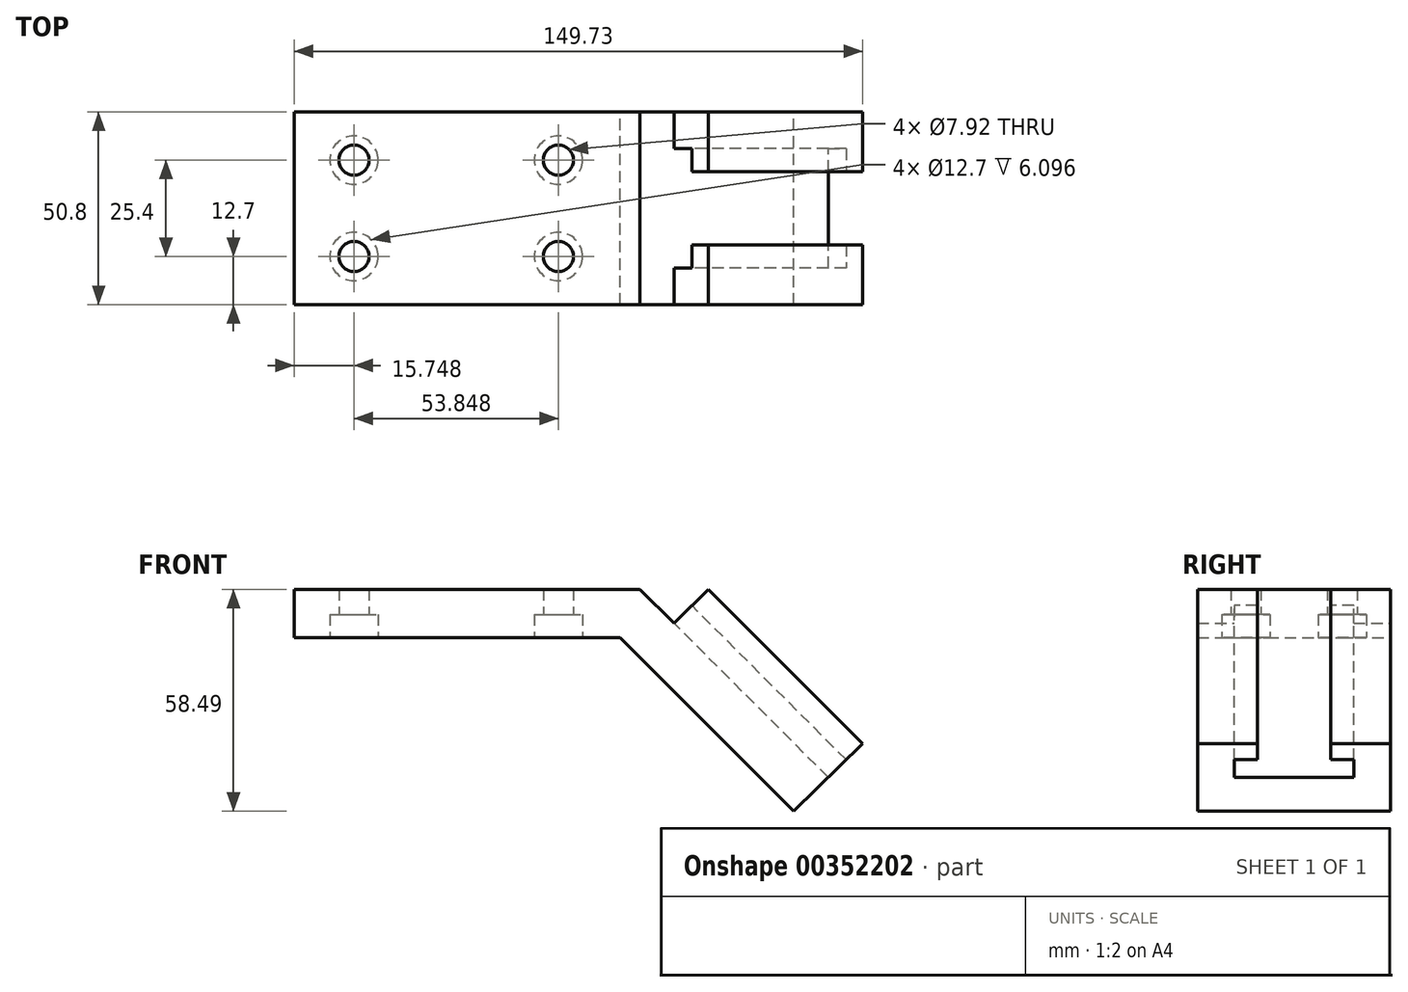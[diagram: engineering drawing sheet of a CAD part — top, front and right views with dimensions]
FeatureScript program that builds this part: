
annotation { "Feature Type Name" : "Feature", "Feature Type Description" : "" }
export const myFeature = defineFeature(function(context is Context, id is Id, definition is map)
    precondition{}
    {
        {
            var Q0;
            Q0=qCreatedBy(makeId("Front.planeOp"),FACE);
            var sketch = newSketch(context, id + "F0", { "sketchPlane" : qUnion([Q0])});
            skLineSegment(sketch, "E0", {"start": v(0, 0) * mm, "end": v(0, 12.7) * mm});
            skLineSegment(sketch, "E1", {"start": v(0, 12.7) * mm, "end": v(91.11, 12.7) * mm});
            skLineSegment(sketch, "E2", {"start": v(0, 0) * mm, "end": v(85.85, 0) * mm});
            skLineSegment(sketch, "E3", {"start": v(91.11, 12.7) * mm, "end": v(100.1, 3.72) * mm});
            skLineSegment(sketch, "E4", {"start": v(85.85, 0) * mm, "end": v(131.64, -45.79) * mm});
            skLineSegment(sketch, "E5", {"start": v(149.73, -27.96) * mm, "end": v(109.07, 12.7) * mm});
            skLineSegment(sketch, "E6", {"start": v(109.07, 12.7) * mm, "end": v(100.1, 3.72) * mm});
            skLineSegment(sketch, "E7", {"start": v(131.64, -45.79) * mm, "end": v(149.73, -27.96) * mm});
            skSolve(sketch);
        }
        {
            var Q0;
            Q0=makeQuery(id+"F0.imprint","IMPRINT",FACE,{"disambiguationData":[TD([[makeQuery(id+"F0.imprint","IMPRINT",EDGE,{"derivedFrom":sQuery(id+"F0.wireOp",EDGE,"E0")}),-1.0]])]});
            extrude(context, id + "F1", {"entities" : qUnion([Q0]), "depth" : 50.8 * mm});
        }
        {
            var Q0;
            Q0=qCreatedBy(makeId("Top.planeOp"),FACE);
            var sketch = newSketch(context, id + "F2", { "sketchPlane" : qUnion([Q0])});
            skCircle(sketch, "E8", {"center": v(15.75, -12.7) * mm, "radius": 3.96 * mm});
            skCircle(sketch, "E9", {"center": v(15.75, -38.1) * mm, "radius": 3.96 * mm});
            skCircle(sketch, "E10", {"center": v(69.6, -12.7) * mm, "radius": 3.96 * mm});
            skCircle(sketch, "E11", {"center": v(69.6, -38.1) * mm, "radius": 3.96 * mm});
            skSolve(sketch);
        }
        {
            var Q0;
            Q0=sQuery(id+"F2.wireOp",VERTEX,"E8.center");
            var Q1;
            Q1=sQuery(id+"F2.wireOp",VERTEX,"E9.center");
            var Q2;
            Q2=sQuery(id+"F2.wireOp",VERTEX,"E11.center");
            var Q3;
            Q3=sQuery(id+"F2.wireOp",VERTEX,"E10.center");
            var Q4;
            Q4=makeQuery(id+"F1.opExtrude","SWEPT_BODY",BODY,{"disambiguationData":[OSD([sQuery(id+"F0.wireOp",EDGE,"E0"),sQuery(id+"F0.wireOp",EDGE,"E1"),sQuery(id+"F0.wireOp",EDGE,"E2"),sQuery(id+"F0.wireOp",EDGE,"E3"),sQuery(id+"F0.wireOp",EDGE,"E4"),sQuery(id+"F0.wireOp",EDGE,"E5"),sQuery(id+"F0.wireOp",EDGE,"E6"),sQuery(id+"F0.wireOp",EDGE,"E7")])]});
            hole(context, id + "F3", {"style" : HoleStyle.C_BORE, "endStyle" : HoleEndStyle.THROUGH, "oppositeDirection" : true, "holeDiameter" : 7.92 * mm, "cBoreDiameter" : 12.7 * mm, "cBoreDepth" : 6.1 * mm, "isTappedThrough" : true, "tappedDepth" : 12.7 * mm, "tapClearance" : 3, "locations" : qUnion([Q0, Q1, Q2, Q3]), "scope" : qUnion([Q4])});
        }
        {
            var Q0;
            Q0=makeQuery(id+"F1.opExtrude","SWEPT_FACE",FACE,{"disambiguationData":[OSD([sQuery(id+"F0.wireOp",EDGE,"E5")])]});
            var sketch = newSketch(context, id + "F4", { "sketchPlane" : qUnion([Q0])});
            skArc(sketch, "E12", {"start": v(115.63, -50.8) * mm, "mid": v(122, -25.4) * mm, "end": v(115.63, 0) * mm});
            skLineSegment(sketch, "E13", {"start": v(115.63, -50.8) * mm, "end": v(125.64, -50.8) * mm});
            skLineSegment(sketch, "E14", {"start": v(125.64, -50.8) * mm, "end": v(125.64, 0) * mm});
            skLineSegment(sketch, "E15", {"start": v(125.64, 0) * mm, "end": v(115.63, 0) * mm});
            skSolve(sketch);
        }
        {
            var Q0;
            Q0 = qSketchRegion(id + "F4", true);
            extrude(context, id + "F5", {"entities" : qUnion([Q0]), "operationType" : NewBodyOperationType.REMOVE, "endBound" : BoundingType.THROUGH_ALL, "oppositeDirection" : true, "depth" : 25.4 * mm});
        }
        {
            var Q0;
            Q0=makeQuery(id+"F1.opExtrude","SWEPT_FACE",FACE,{"disambiguationData":[OSD([sQuery(id+"F0.wireOp",EDGE,"E6")])]});
            var sketch = newSketch(context, id + "F6", { "sketchPlane" : qUnion([Q0])});
            skLineSegment(sketch, "E16", {"start": v(41.15, 73.4) * mm, "end": v(9.65, 73.4) * mm});
            skLineSegment(sketch, "E17", {"start": v(9.65, 73.4) * mm, "end": v(9.65, 80) * mm});
            skLineSegment(sketch, "E18", {"start": v(9.65, 80) * mm, "end": v(15.75, 80) * mm});
            skLineSegment(sketch, "E19", {"start": v(15.75, 80) * mm, "end": v(15.75, 86.1) * mm});
            skLineSegment(sketch, "E20", {"start": v(15.75, 86.1) * mm, "end": v(35.05, 86.1) * mm});
            skLineSegment(sketch, "E21", {"start": v(35.05, 86.1) * mm, "end": v(35.05, 80) * mm});
            skLineSegment(sketch, "E22", {"start": v(35.05, 80) * mm, "end": v(41.15, 80) * mm});
            skLineSegment(sketch, "E23", {"start": v(41.15, 80) * mm, "end": v(41.15, 73.4) * mm});
            skSolve(sketch);
        }
        {
            var Q0;
            Q0 = qSketchRegion(id + "F6", true);
            extrude(context, id + "F7", {"entities" : qUnion([Q0]), "operationType" : NewBodyOperationType.REMOVE, "endBound" : BoundingType.THROUGH_ALL, "oppositeDirection" : true, "depth" : 25.4 * mm});
        }
    });
